# Revit family: QF_ELECTROLUXPROFESSIONAL_589467_MC0ACAHOBO
name_source: partatom
category: Specialty Equipment
revit_build: Autodesk Revit 2018 (Build: 20190510_1515(x64)
units: mm (PartAtom-declared; Revit-internal decimal feet)

## family parameters
Always vertical = Yes
Cut with Voids When Loaded = No
Part Type = Normal
Room Calculation Point = No
Round Connector Dimension = Use Diameter
Shared = No
Work Plane-Based = No

## types (1)
- QF_ELECTROLUXPROFESSIONAL_589467_MC0ACAHOBO
    Apparent Power = 1000 VA
    Conn Conduit = Yes
    Cycle = 50 Hz
    Description = HOLDING CAB,GN,2 DRAW,1S,800X900X450H
    Direct Waste Size = 0"
    Elec Conn Connection Height = 0 mm  [stored 0 ft]
    Electrical Remarks = 230 V/1N ph/50 Hz
    FL Amps = 4 A
    HP = 1.3 HP
    Manufacturer = ELECTROLUX
    Max Overcurrent Protection = 0 A
    Min Ckt Ampacity = 0 A
    Model = 589467
    Phase = 1
    Volts = 230 V
    Watts = 1000 W
    Weight in Pounds = 97
    Width = 800 mm  [stored 2.62467 ft]

note: [stored X ft] marks values corroborated as IEEE doubles in the binary element streams (Revit-internal decimal feet)

## geometry (parser evidence)
native form markers: Blend x34, Sweep x8
no freeform markers — native parametric forms only
